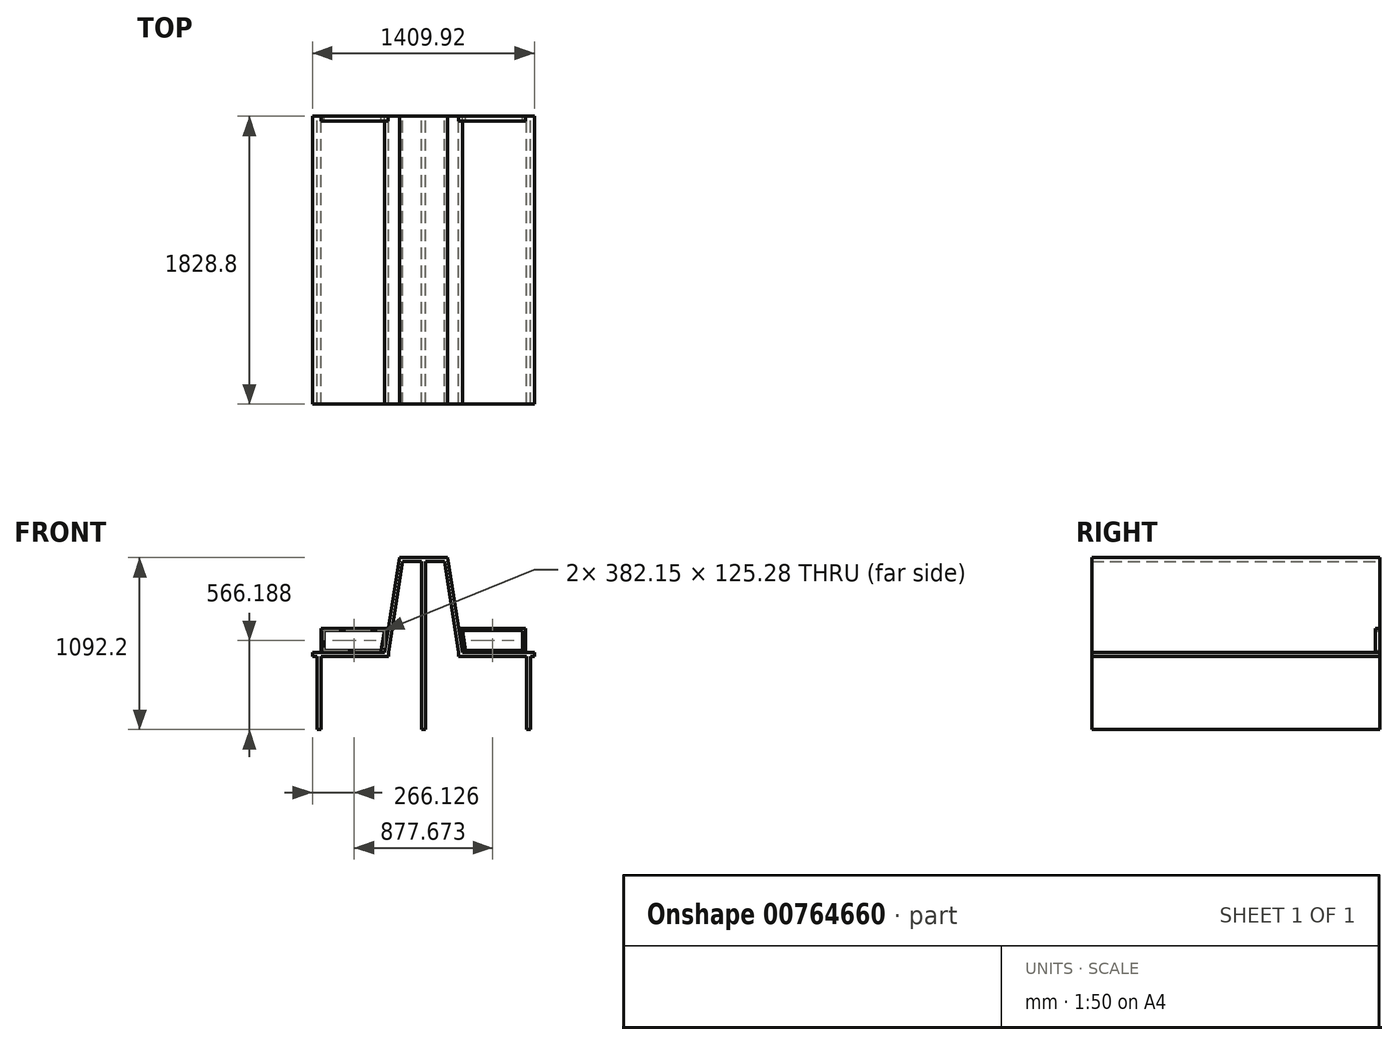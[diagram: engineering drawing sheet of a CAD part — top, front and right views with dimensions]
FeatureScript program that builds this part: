
annotation { "Feature Type Name" : "Feature", "Feature Type Description" : "" }
export const myFeature = defineFeature(function(context is Context, id is Id, definition is map)
    precondition{}
    {
        {
            var Q0;
            Q0=qCreatedBy(makeId("Front.planeOp"),FACE);
            var sketch = newSketch(context, id + "F0", { "sketchPlane" : qUnion([Q0])});
            skLineSegment(sketch, "E0", {"start": v(95.36, 57.36) * mm, "end": v(0, -544.73) * mm});
            skLineSegment(sketch, "E1", {"start": v(0, -544.73) * mm, "end": v(-457.2, -544.73) * mm});
            skLineSegment(sketch, "E2", {"start": v(24.14, -392.33) * mm, "end": v(-402.58, -392.33) * mm});
            skLineSegment(sketch, "E3", {"start": v(-402.58, -392.33) * mm, "end": v(-402.58, -544.73) * mm});
            skLineSegment(sketch, "E4", {"start": v(95.36, 57.36) * mm, "end": v(400.16, 57.36) * mm});
            skLineSegment(sketch, "E5", {"start": v(247.76, 176.97) * mm, "end": v(247.76, -780.96) * mm, "construction": true});
            skPoint(sketch, "E5.startSnap0", {"position": v(247.76, 57.36) * mm});
            skLineSegment(sketch, "E6.MirrorCS", {"start": v(400.16, 57.36) * mm, "end": v(95.36, 57.36) * mm});
            skLineSegment(sketch, "E7.MirrorCS", {"start": v(400.16, 57.36) * mm, "end": v(495.52, -544.73) * mm});
            skLineSegment(sketch, "E8.MirrorCS", {"start": v(471.39, -392.33) * mm, "end": v(898.1, -392.33) * mm});
            skLineSegment(sketch, "E9.MirrorCS", {"start": v(495.52, -544.73) * mm, "end": v(952.72, -544.73) * mm});
            skLineSegment(sketch, "E10.MirrorCS", {"start": v(898.1, -392.33) * mm, "end": v(898.1, -544.73) * mm});
            skLineSegment(sketch, "E11", {"start": v(-457.2, -544.73) * mm, "end": v(-457.2, -570.13) * mm});
            skLineSegment(sketch, "E12", {"start": v(-457.2, -570.13) * mm, "end": v(0, -570.13) * mm});
            skLineSegment(sketch, "E13", {"start": v(0, -570.13) * mm, "end": v(0, -544.73) * mm});
            skLineSegment(sketch, "E14", {"start": v(0, -544.73) * mm, "end": v(25.4, -544.73) * mm});
            skLineSegment(sketch, "E15", {"start": v(25.4, -544.73) * mm, "end": v(116.74, 31.96) * mm});
            skLineSegment(sketch, "E16", {"start": v(116.74, 31.96) * mm, "end": v(382.46, 31.96) * mm});
            skLineSegment(sketch, "E17", {"start": v(382.46, 31.96) * mm, "end": v(470.12, -544.73) * mm});
            skLineSegment(sketch, "E18", {"start": v(470.12, -544.73) * mm, "end": v(495.52, -544.73) * mm});
            skLineSegment(sketch, "E19", {"start": v(25.4, -544.73) * mm, "end": v(25.4, -570.13) * mm});
            skLineSegment(sketch, "E20", {"start": v(25.4, -570.13) * mm, "end": v(0, -570.13) * mm});
            skLineSegment(sketch, "E21", {"start": v(470.12, -544.73) * mm, "end": v(470.12, -570.13) * mm});
            skLineSegment(sketch, "E22", {"start": v(470.12, -570.13) * mm, "end": v(952.72, -570.13) * mm});
            skLineSegment(sketch, "E23", {"start": v(362.74, 57.36) * mm, "end": v(362.74, 31.96) * mm});
            skLineSegment(sketch, "E24", {"start": v(145.92, 57.36) * mm, "end": v(145.92, 31.96) * mm});
            skLineSegment(sketch, "E25", {"start": v(952.72, -544.73) * mm, "end": v(952.72, -570.13) * mm});
            skLineSegment(sketch, "E26", {"start": v(235.06, 31.96) * mm, "end": v(235.06, -1034.84) * mm});
            skLineSegment(sketch, "E27.MirrorCS", {"start": v(260.46, 31.96) * mm, "end": v(260.46, -1034.84) * mm});
            skLineSegment(sketch, "E28", {"start": v(235.06, -1034.84) * mm, "end": v(260.46, -1034.84) * mm});
            skLineSegment(sketch, "E29", {"start": v(903.19, -570.13) * mm, "end": v(903.19, -1034.84) * mm});
            skLineSegment(sketch, "E30", {"start": v(928.59, -570.13) * mm, "end": v(928.59, -1034.84) * mm});
            skLineSegment(sketch, "E31", {"start": v(903.19, -1034.84) * mm, "end": v(928.59, -1034.84) * mm});
            skLineSegment(sketch, "E32", {"start": v(-402.58, -570.13) * mm, "end": v(-402.58, -1034.84) * mm});
            skLineSegment(sketch, "E33", {"start": v(-402.58, -1034.84) * mm, "end": v(-427.98, -1034.84) * mm});
            skLineSegment(sketch, "E34", {"start": v(-427.98, -1034.84) * mm, "end": v(-427.98, -570.13) * mm});
            skLineSegment(sketch, "E35", {"start": v(0, -406.01) * mm, "end": v(-19.84, -531.3) * mm});
            skLineSegment(sketch, "E36", {"start": v(-19.84, -531.3) * mm, "end": v(-382.15, -531.3) * mm});
            skLineSegment(sketch, "E37", {"start": v(-382.15, -531.3) * mm, "end": v(-382.15, -406.86) * mm});
            skLineSegment(sketch, "E38", {"start": v(-382.15, -406.86) * mm, "end": v(0, -406.01) * mm});
            skLineSegment(sketch, "E39.MirrorCS", {"start": v(877.67, -406.86) * mm, "end": v(495.52, -406.01) * mm});
            skLineSegment(sketch, "E40.MirrorCS", {"start": v(495.52, -406.01) * mm, "end": v(515.37, -531.3) * mm});
            skLineSegment(sketch, "E41.MirrorCS", {"start": v(515.37, -531.3) * mm, "end": v(877.67, -531.3) * mm});
            skLineSegment(sketch, "E42.MirrorCS", {"start": v(877.67, -531.3) * mm, "end": v(877.67, -406.86) * mm});
            skSolve(sketch);
        }
        {
            var Q0;
            {var subQ0=sQuery(id+"F0.wireOp",EDGE,"E32");Q0=makeQuery(id+"F0.imprint","IMPRINT",FACE,{"disambiguationData":[TD([[makeQuery(id+"F0.imprint","IMPRINT",EDGE,{"derivedFrom":subQ0}),-1.0]])]});}
            var Q1;
            {var subQ0=sQuery(id+"F0.wireOp",EDGE,"E26");Q1=makeQuery(id+"F0.imprint","IMPRINT",FACE,{"disambiguationData":[TD([[makeQuery(id+"F0.imprint","IMPRINT",EDGE,{"derivedFrom":subQ0}),1.0]])]});}
            var Q2;
            {var subQ0=sQuery(id+"F0.wireOp",EDGE,"E29");Q2=makeQuery(id+"F0.imprint","IMPRINT",FACE,{"disambiguationData":[TD([[makeQuery(id+"F0.imprint","IMPRINT",EDGE,{"derivedFrom":subQ0}),1.0]])]});}
            var Q3;
            Q3=makeQuery(id+"F0.imprint","IMPRINT",FACE,{"disambiguationData":[TD([[makeQuery(id+"F0.imprint","IMPRINT",EDGE,{"derivedFrom":sQuery(id+"F0.wireOp",EDGE,"E13")}),-1.0]])]});
            var Q4;
            {var subQ0=sQuery(id+"F0.wireOp",EDGE,"E14");Q4=makeQuery(id+"F0.imprint","IMPRINT",FACE,{"disambiguationData":[TD([[makeQuery(id+"F0.imprint","IMPRINT",EDGE,{"derivedFrom":subQ0}),1.0]])]});}
            var Q5;
            {var subQ5=sQuery(id+"F0.wireOp",EDGE,"nvqRZboN-uEvF-tkn8-jJZU-JW9SNXs5QeY9");Q5=makeQuery(id+"F0.imprint","IMPRINT",FACE,{"disambiguationData":[TD([[makeQuery(id+"F0.imprint","IMPRINT",EDGE,{"derivedFrom":subQ5}),-1.0]])]});}
            var Q6;
            {var subQ3=sQuery(id+"F0.wireOp",EDGE,"nvqRZboN-uEvF-tkn8-jJZU-JW9SNXs5QeY9");Q6=makeQuery(id+"F0.imprint","IMPRINT",FACE,{"disambiguationData":[TD([[makeQuery(id+"F0.imprint","IMPRINT",EDGE,{"derivedFrom":subQ3}),1.0]])]});}
            var Q7;
            {var subQ5=sQuery(id+"F0.wireOp",EDGE,"u9E9bbab-mqrn-U2ln-aYJZ-kViFr79o4hRc");Q7=makeQuery(id+"F0.imprint","IMPRINT",FACE,{"disambiguationData":[TD([[makeQuery(id+"F0.imprint","IMPRINT",EDGE,{"derivedFrom":subQ5}),-1.0]])]});}
            var Q8;
            {var subQ0=sQuery(id+"F0.wireOp",EDGE,"E23");Q8=makeQuery(id+"F0.imprint","IMPRINT",FACE,{"disambiguationData":[TD([[makeQuery(id+"F0.imprint","IMPRINT",EDGE,{"derivedFrom":subQ0}),-1.0]])]});}
            var Q9;
            {var subQ4=sQuery(id+"F0.wireOp",EDGE,"E18");Q9=makeQuery(id+"F0.imprint","IMPRINT",FACE,{"disambiguationData":[TD([[makeQuery(id+"F0.imprint","IMPRINT",EDGE,{"derivedFrom":subQ4}),-1.0]])]});}
            var Q10;
            {var subQ7=sQuery(id+"F0.wireOp",EDGE,"E17");Q10=makeQuery(id+"F0.imprint","IMPRINT",FACE,{"disambiguationData":[TD([[makeQuery(id+"F0.imprint","IMPRINT",EDGE,{"derivedFrom":subQ7}),1.0]])]});}
            var Q11;
            {var subQ1=sQuery(id+"F0.wireOp",EDGE,"E11");Q11=makeQuery(id+"F0.imprint","IMPRINT",FACE,{"disambiguationData":[TD([[makeQuery(id+"F0.imprint","IMPRINT",EDGE,{"derivedFrom":subQ1}),1.0]])]});}
            extrude(context, id + "F1", {"entities" : qUnion([Q0, Q1, Q2, Q3, Q4, Q5, Q6, Q7, Q8, Q9, Q10, Q11]), "depth" : 1828.8 * mm, "offsetDistance" : 25.4 * mm});
        }
        {
            var Q0;
            {var subQ1=sQuery(id+"F0.wireOp",EDGE,"E2");Q0=makeQuery(id+"F0.imprint","IMPRINT",FACE,{"disambiguationData":[TD([[makeQuery(id+"F0.imprint","IMPRINT",EDGE,{"derivedFrom":subQ1}),1.0]])]});}
            var Q1;
            {var subQ4=sQuery(id+"F0.wireOp",EDGE,"E8.MirrorCS");Q1=makeQuery(id+"F0.imprint","IMPRINT",FACE,{"disambiguationData":[TD([[makeQuery(id+"F0.imprint","IMPRINT",EDGE,{"derivedFrom":subQ4}),-1.0]])]});}
            extrude(context, id + "F2", {"entities" : qUnion([Q0, Q1]), "operationType" : NewBodyOperationType.ADD, "depth" : 30 * mm, "offsetDistance" : 25.4 * mm});
        }
    });
